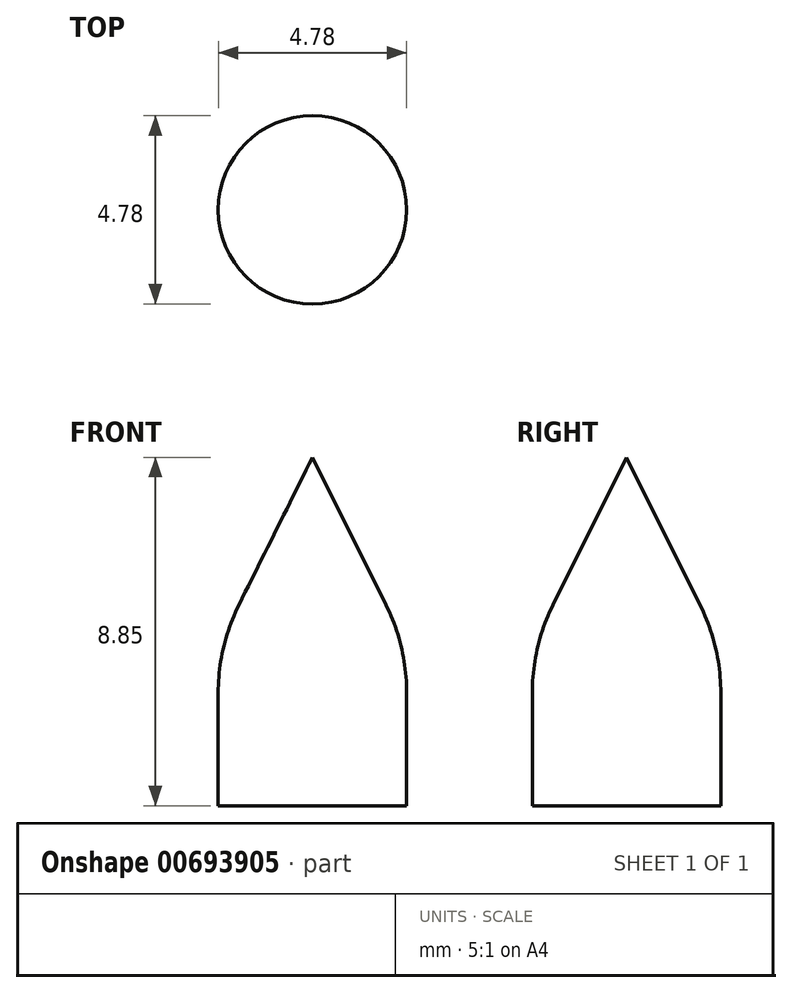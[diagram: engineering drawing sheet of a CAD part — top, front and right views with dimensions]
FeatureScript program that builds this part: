
annotation { "Feature Type Name" : "Feature", "Feature Type Description" : "" }
export const myFeature = defineFeature(function(context is Context, id is Id, definition is map)
    precondition{}
    {
        {
            var Q0;
            Q0=qCreatedBy(makeId("Right.planeOp"),FACE);
            var sketch = newSketch(context, id + "F0", { "sketchPlane" : qUnion([Q0])});
            skLineSegment(sketch, "E0", {"start": v(0, 0) * mm, "end": v(-2.4, 0) * mm});
            skLineSegment(sketch, "E1", {"start": v(-2.4, 0) * mm, "end": v(-2.4, 4.05) * mm});
            skLineSegment(sketch, "E2", {"start": v(-2.4, 4.05) * mm, "end": v(0, 8.85) * mm});
            skLineSegment(sketch, "E3", {"start": v(0, 8.85) * mm, "end": v(0, 0) * mm});
            skSolve(sketch);
        }
        {
            var Q0;
            Q0=makeQuery(id+"F0.imprint","IMPRINT",FACE,{"disambiguationData":[TD([[makeQuery(id+"F0.imprint","IMPRINT",EDGE,{"derivedFrom":sQuery(id+"F0.wireOp",EDGE,"E0")}),-1.0]])]});
            var Q1;
            Q1=sQuery(id+"F0.wireOp",EDGE,"E3");
            revolve(context, id + "F1", {"entities" : qUnion([Q0]), "axis" : qUnion([Q1]), "revolveType" : RevolveType.FULL});
        }
        {
            var Q0;
            Q0=makeQuery(id+"F1.opRevolve","SWEPT_EDGE",EDGE,{"disambiguationData":[OSD([sQuery(id+"F0.wireOp",EDGE,"E1"),sQuery(id+"F0.wireOp",EDGE,"E2")])]});
            fillet(context, id + "F2", {"entities" : qUnion([Q0]), "radius" : 5 * mm, "tangentPropagation" : true, "allowEdgeOverflow" : false});
        }
    });
